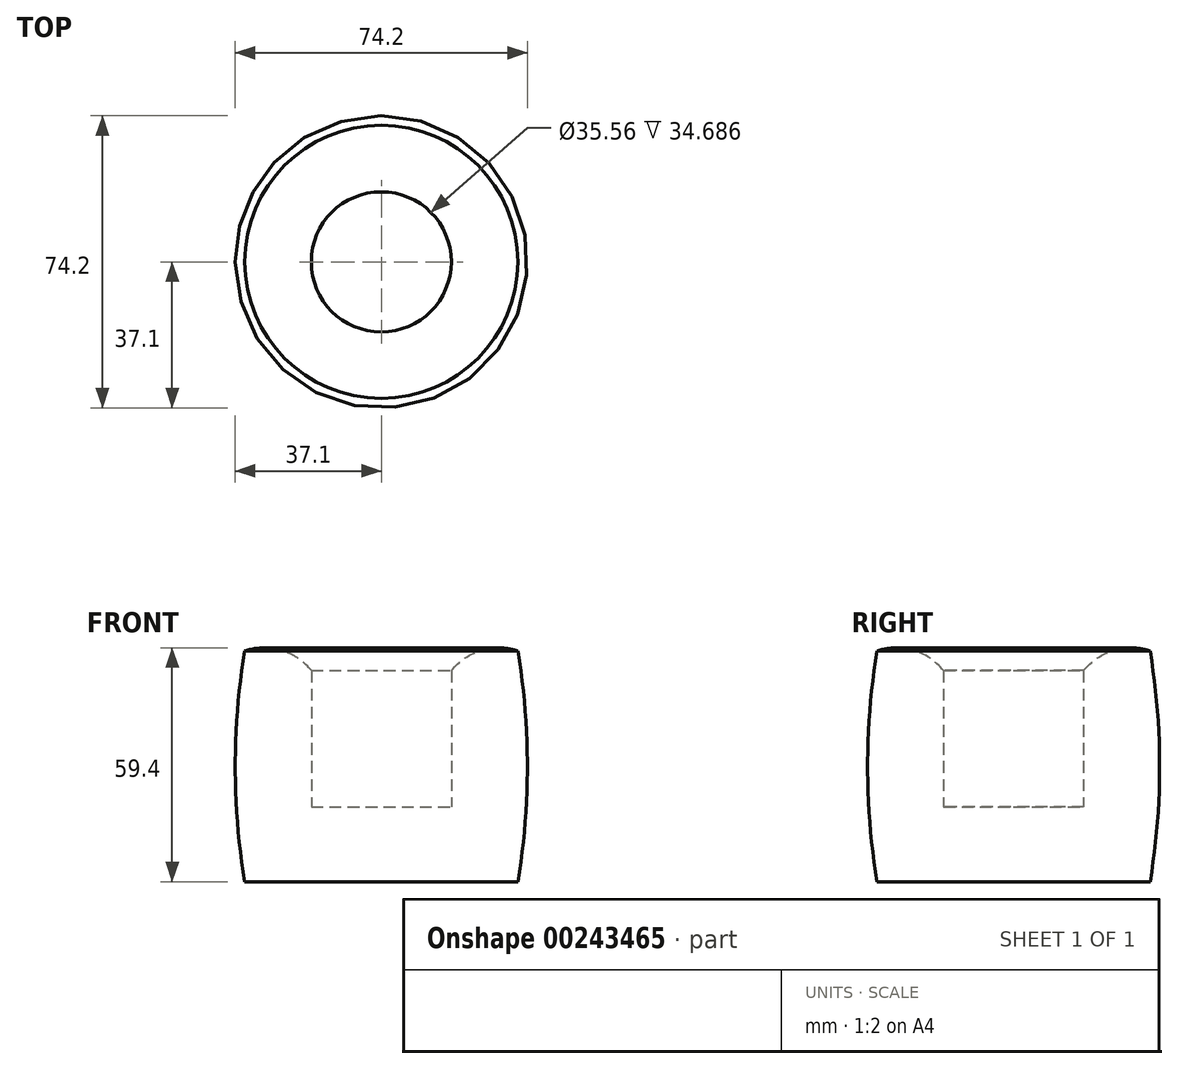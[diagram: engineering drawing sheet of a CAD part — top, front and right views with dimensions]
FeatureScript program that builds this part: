
annotation { "Feature Type Name" : "Feature", "Feature Type Description" : "" }
export const myFeature = defineFeature(function(context is Context, id is Id, definition is map)
    precondition{}
    {
        {
            var Q0;
            Q0=qCreatedBy(makeId("Front.planeOp"),FACE);
            var sketch = newSketch(context, id + "F0", { "sketchPlane" : qUnion([Q0])});
            skLineSegment(sketch, "E0", {"start": v(0, 8.3) * mm, "end": v(-17.78, 8.3) * mm});
            skLineSegment(sketch, "E1", {"start": v(-17.78, 8.3) * mm, "end": v(-17.78, 43) * mm});
            skArc(sketch, "E2", {"start": v(-17.78, 43) * mm, "mid": v(-25.45, 48.14) * mm, "end": v(-34.69, 47.95) * mm});
            skArc(sketch, "E3", {"start": v(-34.69, 47.95) * mm, "mid": v(-37.1, 18.65) * mm, "end": v(-34.69, -10.64) * mm});
            skLineSegment(sketch, "E4", {"start": v(-34.69, -10.64) * mm, "end": v(0, -10.64) * mm});
            skLineSegment(sketch, "E5", {"start": v(0, -10.64) * mm, "end": v(0, 8.3) * mm});
            skSolve(sketch);
        }
        {
            var Q0;
            Q0=makeQuery(id+"F0.imprint","IMPRINT",FACE,{"disambiguationData":[TD([[makeQuery(id+"F0.imprint","IMPRINT",EDGE,{"derivedFrom":sQuery(id+"F0.wireOp",EDGE,"E0")}),1.0]])]});
            var Q1;
            Q1=sQuery(id+"F0.wireOp",EDGE,"E5");
            revolve(context, id + "F1", {"entities" : qUnion([Q0]), "axis" : qUnion([Q1]), "revolveType" : RevolveType.FULL});
        }
    });
